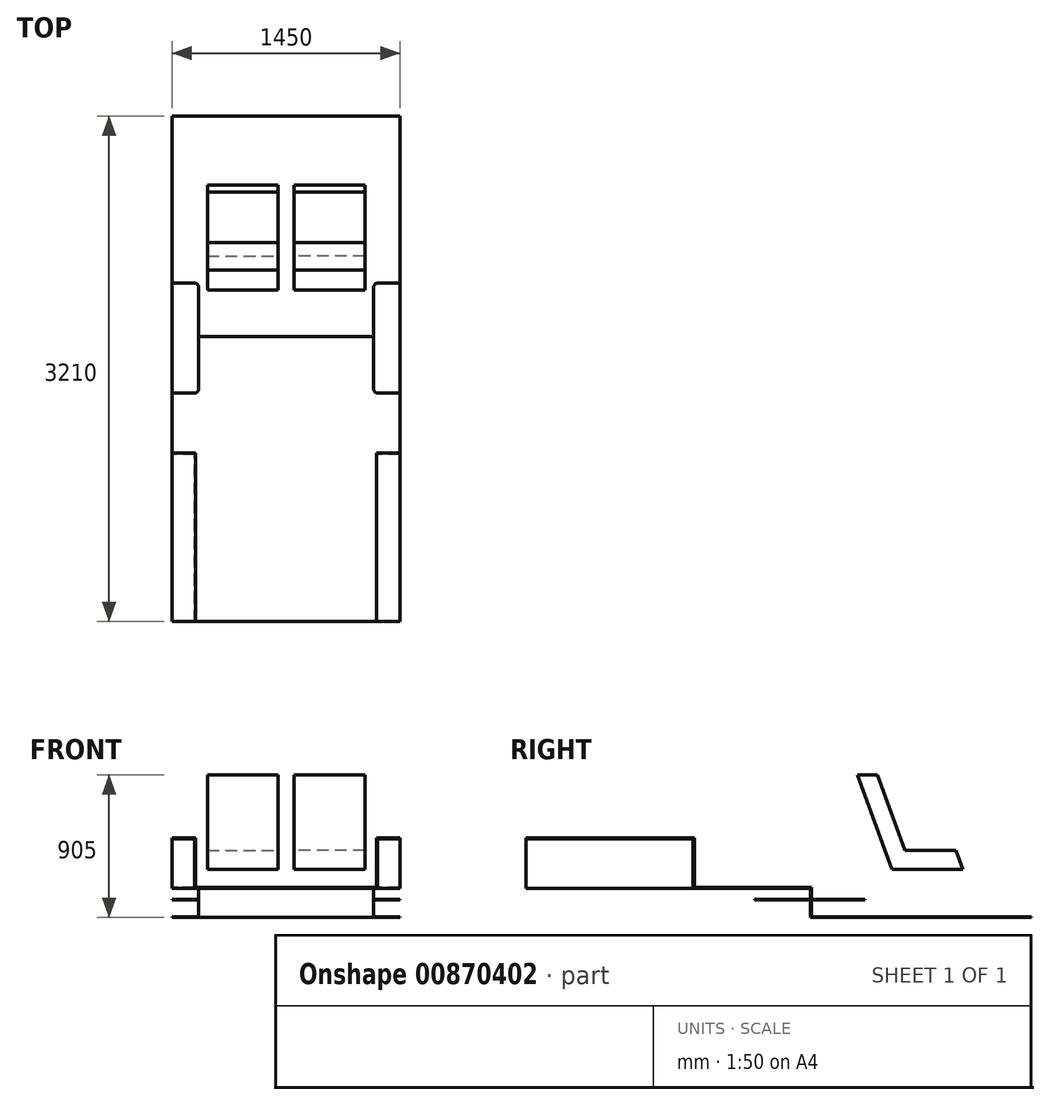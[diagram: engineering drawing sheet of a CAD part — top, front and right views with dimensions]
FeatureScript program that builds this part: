
annotation { "Feature Type Name" : "Feature", "Feature Type Description" : "" }
export const myFeature = defineFeature(function(context is Context, id is Id, definition is map)
    precondition{}
    {
        {
            var Q0;
            Q0=qCreatedBy(makeId("Front.planeOp"),FACE);
            cPlane(context, id + "F0", {"entities" : qUnion([Q0]), "cplaneType" : CPlaneType.OFFSET, "offset" : 750 * mm, "oppositeDirection" : true, "width" : 150 * mm, "height" : 150 * mm});
        }
        {
            var Q0;
            Q0=qCreatedBy(makeId("Front.planeOp"),FACE);
            cPlane(context, id + "F1", {"entities" : qUnion([Q0]), "cplaneType" : CPlaneType.OFFSET, "offset" : 1400 * mm, "width" : 150 * mm, "height" : 150 * mm});
        }
        {
            var Q0;
            Q0=qCreatedBy(makeId("Front.planeOp"),FACE);
            var sketch = newSketch(context, id + "F2", { "sketchPlane" : qUnion([Q0])});
            skLineSegment(sketch, "E0", {"start": v(-725, 0) * mm, "end": v(-575, 0) * mm});
            skLineSegment(sketch, "E1", {"start": v(-575, 0) * mm, "end": v(-575, -315) * mm});
            skLineSegment(sketch, "E2", {"start": v(-575, -315) * mm, "end": v(0, -315) * mm});
            skLineSegment(sketch, "E3", {"start": v(0, 0) * mm, "end": v(0, -315) * mm, "construction": true});
            skLineSegment(sketch, "E4.MirrorCS", {"start": v(575, 0) * mm, "end": v(575, -315) * mm});
            skLineSegment(sketch, "E5.MirrorCS", {"start": v(575, -315) * mm, "end": v(0, -315) * mm});
            skLineSegment(sketch, "E6.MirrorCS", {"start": v(725, 0) * mm, "end": v(575, 0) * mm});
            skLineSegment(sketch, "E7.0", {"start": v(725, -5) * mm, "end": v(580, -5) * mm});
            skLineSegment(sketch, "E7.1", {"start": v(580, -5) * mm, "end": v(580, -320) * mm});
            skLineSegment(sketch, "E7.2", {"start": v(-725, -5) * mm, "end": v(-580, -5) * mm});
            skLineSegment(sketch, "E7.3", {"start": v(-580, -5) * mm, "end": v(-580, -320) * mm});
            skLineSegment(sketch, "E7.4", {"start": v(-580, -320) * mm, "end": v(0, -320) * mm});
            skLineSegment(sketch, "E7.5", {"start": v(580, -320) * mm, "end": v(0, -320) * mm});
            skLineSegment(sketch, "E8", {"start": v(-725, -5) * mm, "end": v(-725, 0) * mm});
            skLineSegment(sketch, "E9", {"start": v(725, -5) * mm, "end": v(725, 0) * mm});
            skSolve(sketch);
        }
        {
            var Q0;
            Q0=makeQuery(id+"F2.imprint","IMPRINT",FACE,{"disambiguationData":[TD([[makeQuery(id+"F2.imprint","IMPRINT",EDGE,{"derivedFrom":sQuery(id+"F2.wireOp",EDGE,"E0")}),-1.0]])]});
            extrude(context, id + "F3", {"entities" : qUnion([Q0]), "depth" : 1060 * mm, "offsetDistance" : 25 * mm});
        }
        {
            var Q0;
            Q0=makeQuery(id+"F3.opExtrude","CAP_FACE",FACE,{"disambiguationData":[OSD([sQuery(id+"F2.wireOp",EDGE,"E0"),sQuery(id+"F2.wireOp",EDGE,"E1"),sQuery(id+"F2.wireOp",EDGE,"E2"),sQuery(id+"F2.wireOp",EDGE,"E4.MirrorCS"),sQuery(id+"F2.wireOp",EDGE,"E5.MirrorCS"),sQuery(id+"F2.wireOp",EDGE,"E6.MirrorCS"),sQuery(id+"F2.wireOp",EDGE,"E7.0"),sQuery(id+"F2.wireOp",EDGE,"E7.1"),sQuery(id+"F2.wireOp",EDGE,"E7.2"),sQuery(id+"F2.wireOp",EDGE,"E7.3"),sQuery(id+"F2.wireOp",EDGE,"E7.4"),sQuery(id+"F2.wireOp",EDGE,"E7.5"),sQuery(id+"F2.wireOp",EDGE,"E8"),sQuery(id+"F2.wireOp",EDGE,"E9")])],"isStart":true});
            var sketch = newSketch(context, id + "F4", { "sketchPlane" : qUnion([Q0])});
            skLineSegment(sketch, "E10", {"start": v(-725, 0) * mm, "end": v(-725, -320) * mm});
            skLineSegment(sketch, "E11", {"start": v(-725, -320) * mm, "end": v(725, -320) * mm});
            skLineSegment(sketch, "E12", {"start": v(725, -320) * mm, "end": v(725, 0) * mm});
            skLineSegment(sketch, "E13", {"start": v(725, 0) * mm, "end": v(575, 0) * mm});
            skLineSegment(sketch, "E14", {"start": v(575, 0) * mm, "end": v(575, -315) * mm});
            skLineSegment(sketch, "E15", {"start": v(575, -315) * mm, "end": v(-575, -315) * mm});
            skLineSegment(sketch, "E16", {"start": v(-575, -315) * mm, "end": v(-575, 0) * mm});
            skLineSegment(sketch, "E17", {"start": v(-575, 0) * mm, "end": v(-725, 0) * mm});
            skSolve(sketch);
        }
        {
            var Q0;
            Q0 = qSketchRegion(id + "F4", true);
            extrude(context, id + "F5", {"entities" : qUnion([Q0]), "operationType" : NewBodyOperationType.ADD, "depth" : 10 * mm, "offsetDistance" : 25 * mm});
        }
        {
            var Q0;
            Q0=makeQuery(id+"F5.opExtrude","CAP_FACE",FACE,{"disambiguationData":[OSD([sQuery(id+"F4.wireOp",EDGE,"E10"),sQuery(id+"F4.wireOp",EDGE,"E11"),sQuery(id+"F4.wireOp",EDGE,"E12"),sQuery(id+"F4.wireOp",EDGE,"E13"),sQuery(id+"F4.wireOp",EDGE,"E14"),sQuery(id+"F4.wireOp",EDGE,"E15"),sQuery(id+"F4.wireOp",EDGE,"E16"),sQuery(id+"F4.wireOp",EDGE,"E17")])],"isStart":false});
            var sketch = newSketch(context, id + "F6", { "sketchPlane" : qUnion([Q0])});
            skLineSegment(sketch, "E18.bottom", {"start": v(-725, -320) * mm, "end": v(725, -320) * mm});
            skLineSegment(sketch, "E18.top", {"start": v(-725, -315) * mm, "end": v(725, -315) * mm});
            skLineSegment(sketch, "E18.left", {"start": v(-725, -320) * mm, "end": v(-725, -315) * mm});
            skLineSegment(sketch, "E18.right", {"start": v(725, -320) * mm, "end": v(725, -315) * mm});
            skSolve(sketch);
        }
        {
            var Q0;
            Q0 = qSketchRegion(id + "F6", true);
            var Q1;
            Q1=qCreatedBy(id+"F0.planeOp",FACE);
            extrude(context, id + "F7", {"entities" : qUnion([Q0]), "operationType" : NewBodyOperationType.ADD, "endBound" : BoundingType.UP_TO_SURFACE, "depth" : 25 * mm, "endBoundEntityFace" : qUnion([Q1]), "offsetDistance" : 25 * mm});
        }
        {
            var Q0;
            Q0=qCreatedBy(makeId("Top.planeOp"),FACE);
            cPlane(context, id + "F8", {"entities" : qUnion([Q0]), "cplaneType" : CPlaneType.OFFSET, "offset" : 500 * mm, "oppositeDirection" : true, "width" : 150 * mm, "height" : 150 * mm});
        }
        {
            var Q0;
            Q0=qCreatedBy(makeId("Top.planeOp"),FACE);
            cPlane(context, id + "F9", {"entities" : qUnion([Q0]), "cplaneType" : CPlaneType.OFFSET, "offset" : 300 * mm, "oppositeDirection" : true, "width" : 150 * mm, "height" : 150 * mm});
        }
        {
            var Q0;
            Q0=qCreatedBy(makeId("Right.planeOp"),FACE);
            var sketch = newSketch(context, id + "F10", { "sketchPlane" : qUnion([Q0])});
            skLineSegment(sketch, "E19", {"start": v(750, -315) * mm, "end": v(750, -500) * mm});
            skLineSegment(sketch, "E20", {"start": v(750, -500) * mm, "end": v(2150, -500) * mm});
            skLineSegment(sketch, "E21", {"start": v(750, -315) * mm, "end": v(745, -315) * mm});
            skLineSegment(sketch, "E22", {"start": v(745, -315) * mm, "end": v(745, -505) * mm});
            skLineSegment(sketch, "E23", {"start": v(745, -505) * mm, "end": v(2150, -505) * mm});
            skLineSegment(sketch, "E24", {"start": v(2150, -505) * mm, "end": v(2150, -500) * mm});
            skSolve(sketch);
        }
        {
            var Q0;
            Q0=qCreatedBy(makeId("Right.planeOp"),FACE);
            var sketch = newSketch(context, id + "F11", { "sketchPlane" : qUnion([Q0])});
            skLineSegment(sketch, "E25", {"start": v(3466, -500) * mm, "end": v(3466, 197.75) * mm});
            skLineSegment(sketch, "E26", {"start": v(3466, 197.75) * mm, "end": v(2488, 459.8) * mm});
            skLineSegment(sketch, "E27", {"start": v(2488, 459.8) * mm, "end": v(1490, 1036) * mm});
            skLineSegment(sketch, "E28", {"start": v(1490, 1036) * mm, "end": v(-1262.6, 1036) * mm});
            skLineSegment(sketch, "E29", {"start": v(-1262.6, 1036) * mm, "end": v(-1410, 200) * mm});
            skLineSegment(sketch, "E30", {"start": v(-1410, 200) * mm, "end": v(-1410, -500) * mm});
            skLineSegment(sketch, "E31", {"start": v(-1410, -500) * mm, "end": v(3466, -500) * mm});
            skCircle(sketch, "E32", {"center": v(2588, -450) * mm, "radius": 350 * mm});
            skCircle(sketch, "E33", {"center": v(-418, -450) * mm, "radius": 350 * mm});
            skLineSegment(sketch, "E34", {"start": v(-1160, 200) * mm, "end": v(-1160, -500) * mm});
            skLineSegment(sketch, "E35.bottom", {"start": v(390, -500) * mm, "end": v(1090, -500) * mm});
            skLineSegment(sketch, "E35.top", {"start": v(390, 800) * mm, "end": v(1090, 800) * mm});
            skLineSegment(sketch, "E35.left", {"start": v(390, -500) * mm, "end": v(390, 800) * mm});
            skLineSegment(sketch, "E35.right", {"start": v(1090, -500) * mm, "end": v(1090, 800) * mm});
            skLineSegment(sketch, "E36", {"start": v(-1098.9, 915) * mm, "end": v(116.64, 915) * mm});
            skSolve(sketch);
        }
        {
            var Q0;
            Q0=makeQuery(id+"F10.imprint","IMPRINT",FACE,{"disambiguationData":[TD([[makeQuery(id+"F10.imprint","IMPRINT",EDGE,{"derivedFrom":sQuery(id+"F10.wireOp",EDGE,"E19")}),-1.0]])]});
            var Q1;
            Q1=makeQuery(id+"F7.boolean.opBoolean","MERGE",FACE,{"derivedFrom":[makeQuery(id+"F5.boolean.opBoolean","MERGE",FACE,{"derivedFrom":[makeQuery(id+"F3.opExtrude","SWEPT_FACE",FACE,{"disambiguationData":[OSD([sQuery(id+"F2.wireOp",EDGE,"E9")])]}),makeQuery(id+"F5.opExtrude","SWEPT_FACE",FACE,{"disambiguationData":[OSD([sQuery(id+"F4.wireOp",EDGE,"E10")])]})]}),makeQuery(id+"F7.opExtrude","SWEPT_FACE",FACE,{"disambiguationData":[OSD([sQuery(id+"F6.wireOp",EDGE,"E18.left")])]})]});
            var Q2;
            Q2=makeQuery(id+"F7.boolean.opBoolean","MERGE",FACE,{"derivedFrom":[makeQuery(id+"F5.boolean.opBoolean","MERGE",FACE,{"derivedFrom":[makeQuery(id+"F3.opExtrude","SWEPT_FACE",FACE,{"disambiguationData":[OSD([sQuery(id+"F2.wireOp",EDGE,"E8")])]}),makeQuery(id+"F5.opExtrude","SWEPT_FACE",FACE,{"disambiguationData":[OSD([sQuery(id+"F4.wireOp",EDGE,"E12")])]})]}),makeQuery(id+"F7.opExtrude","SWEPT_FACE",FACE,{"disambiguationData":[OSD([sQuery(id+"F6.wireOp",EDGE,"E18.right")])]})]});
            extrude(context, id + "F12", {"entities" : qUnion([Q0]), "operationType" : NewBodyOperationType.ADD, "endBound" : BoundingType.UP_TO_SURFACE, "depth" : 25 * mm, "endBoundEntityFace" : qUnion([Q1]), "offsetDistance" : 25 * mm, "hasSecondDirection" : true, "secondDirectionBound" : SecondDirectionBoundingType.UP_TO_SURFACE, "secondDirectionOppositeDirection" : true, "secondDirectionDepth" : 25 * mm, "secondDirectionBoundEntityFace" : qUnion([Q2])});
        }
        {
            var Q0;
            Q0=qCreatedBy(id+"F9.planeOp",FACE);
            var sketch = newSketch(context, id + "F13", { "sketchPlane" : qUnion([Q0])});
            skLineSegment(sketch, "E37.bottom", {"start": v(725, 390) * mm, "end": v(585, 390) * mm});
            skLineSegment(sketch, "E37.top", {"start": v(725, 1090) * mm, "end": v(585, 1090) * mm});
            skLineSegment(sketch, "E37.left", {"start": v(725, 390) * mm, "end": v(725, 1090) * mm});
            skLineSegment(sketch, "E37.right", {"start": v(555, 420) * mm, "end": v(555, 1060) * mm});
            skPoint(sketch, "E38.visualSharp", {"position": v(555, 390) * mm});
            skArc(sketch, "E38.filletArc", {"start": v(555, 420) * mm, "mid": v(563.79, 398.79) * mm, "end": v(585, 390) * mm});
            skPoint(sketch, "E39.visualSharp", {"position": v(555, 1090) * mm});
            skArc(sketch, "E39.filletArc", {"start": v(585, 1090) * mm, "mid": v(563.79, 1081.21) * mm, "end": v(555, 1060) * mm});
            skArc(sketch, "E40.MirrorCS", {"start": v(-585, 1090) * mm, "mid": v(-563.79, 1081.21) * mm, "end": v(-555, 1060) * mm});
            skArc(sketch, "E41.MirrorCS", {"start": v(-555, 420) * mm, "mid": v(-563.79, 398.79) * mm, "end": v(-585, 390) * mm});
            skPoint(sketch, "E42.MirrorP", {"position": v(-555, 1090) * mm});
            skLineSegment(sketch, "E43.MirrorCS", {"start": v(-555, 420) * mm, "end": v(-555, 1060) * mm});
            skLineSegment(sketch, "E44.MirrorCS", {"start": v(-725, 390) * mm, "end": v(-585, 390) * mm});
            skLineSegment(sketch, "E45.MirrorCS", {"start": v(-725, 390) * mm, "end": v(-725, 1090) * mm});
            skLineSegment(sketch, "E46.MirrorCS", {"start": v(-725, 1090) * mm, "end": v(-585, 1090) * mm});
            skPoint(sketch, "E47.MirrorP", {"position": v(-555, 390) * mm});
            skSolve(sketch);
        }
        {
            var Q0;
            Q0 = qSketchRegion(id + "F13", true);
            var Q1;
            Q1=makeQuery(id+"F12.opExtrude","SWEPT_FACE",FACE,{"disambiguationData":[OSD([sQuery(id+"F10.wireOp",EDGE,"E23")])]});
            extrude(context, id + "F14", {"entities" : qUnion([Q0]), "operationType" : NewBodyOperationType.REMOVE, "endBound" : BoundingType.UP_TO_SURFACE, "oppositeDirection" : true, "depth" : 25 * mm, "endBoundEntityFace" : qUnion([Q1]), "offsetDistance" : 25 * mm});
        }
        {
            var Q0;
            Q0 = qSketchRegion(id + "F13", true);
            var Q1;
            Q1=makeQuery(id+"F7.boolean.opBoolean","MERGE",FACE,{"derivedFrom":[makeQuery(id+"F5.boolean.opBoolean","MERGE",FACE,{"derivedFrom":[makeQuery(id+"F3.opExtrude","SWEPT_FACE",FACE,{"disambiguationData":[OSD([sQuery(id+"F2.wireOp",EDGE,"E2"),sQuery(id+"F2.wireOp",EDGE,"E5.MirrorCS")])]}),makeQuery(id+"F5.opExtrude","SWEPT_FACE",FACE,{"disambiguationData":[OSD([sQuery(id+"F4.wireOp",EDGE,"E15")])]})]}),makeQuery(id+"F7.opExtrude","SWEPT_FACE",FACE,{"disambiguationData":[OSD([sQuery(id+"F6.wireOp",EDGE,"E18.top")])]})]});
            var Q2;
            Q2=makeQuery(id+"F7.boolean.opBoolean","MERGE",FACE,{"derivedFrom":[makeQuery(id+"F5.boolean.opBoolean","MERGE",FACE,{"derivedFrom":[makeQuery(id+"F3.opExtrude","SWEPT_FACE",FACE,{"disambiguationData":[OSD([sQuery(id+"F2.wireOp",EDGE,"E2"),sQuery(id+"F2.wireOp",EDGE,"E5.MirrorCS")])]}),makeQuery(id+"F5.opExtrude","SWEPT_FACE",FACE,{"disambiguationData":[OSD([sQuery(id+"F4.wireOp",EDGE,"E15")])]})]}),makeQuery(id+"F7.opExtrude","SWEPT_FACE",FACE,{"disambiguationData":[OSD([sQuery(id+"F6.wireOp",EDGE,"E18.top")])]})]});
            extrude(context, id + "F15", {"entities" : qUnion([Q0]), "operationType" : NewBodyOperationType.ADD, "endBound" : BoundingType.UP_TO_SURFACE, "oppositeDirection" : true, "depth" : 5 * mm, "endBoundEntityFace" : qUnion([Q1]), "hasOffset" : true, "offsetDistance" : 80 * mm, "offsetOppositeDirection" : true, "hasSecondDirection" : true, "secondDirectionBound" : SecondDirectionBoundingType.UP_TO_SURFACE, "secondDirectionOppositeDirection" : true, "secondDirectionDepth" : 25 * mm, "secondDirectionBoundEntityFace" : qUnion([Q2]), "hasSecondDirectionOffset" : true, "secondDirectionOffsetDistance" : 75 * mm, "secondDirectionOffsetOppositeDirection" : true});
        }
        {
            var Q0;
            Q0=qCreatedBy(makeId("Right.planeOp"),FACE);
            var sketch = newSketch(context, id + "F16", { "sketchPlane" : qUnion([Q0])});
            skLineSegment(sketch, "E48", {"start": v(1043.81, 400) * mm, "end": v(1262.2, -200) * mm});
            skLineSegment(sketch, "E49", {"start": v(1262.2, -200) * mm, "end": v(1712.2, -200) * mm});
            skLineSegment(sketch, "E50", {"start": v(1712.2, -200) * mm, "end": v(1668.52, -80) * mm});
            skLineSegment(sketch, "E51", {"start": v(1668.52, -80) * mm, "end": v(1346.22, -80) * mm});
            skLineSegment(sketch, "E52", {"start": v(1346.22, -80) * mm, "end": v(1171.51, 400) * mm});
            skLineSegment(sketch, "E53", {"start": v(1171.51, 400) * mm, "end": v(1043.81, 400) * mm});
            skSolve(sketch);
        }
        {
            var Q0;
            Q0=makeQuery(id+"F16.imprint","IMPRINT",FACE,{"disambiguationData":[TD([[makeQuery(id+"F16.imprint","IMPRINT",EDGE,{"derivedFrom":sQuery(id+"F16.wireOp",EDGE,"E48")}),1.0]])]});
            var Q1;
            Q1=qCreatedBy(makeId("Right.planeOp"),FACE);
            extrude(context, id + "F17", {"entities" : qUnion([Q0]), "endBound" : BoundingType.UP_TO_SURFACE, "depth" : 25 * mm, "endBoundEntityFace" : qUnion([Q1]), "hasOffset" : true, "offsetDistance" : 500 * mm, "offsetOppositeDirection" : true, "hasSecondDirection" : true, "secondDirectionOppositeDirection" : false, "secondDirectionDepth" : 50 * mm});
        }
        {
            var Q0;
            Q0=makeQuery(id+"F17.opExtrude","SWEPT_BODY",BODY,{"disambiguationData":[OSD([sQuery(id+"F16.wireOp",EDGE,"E48"),sQuery(id+"F16.wireOp",EDGE,"E49"),sQuery(id+"F16.wireOp",EDGE,"E50"),sQuery(id+"F16.wireOp",EDGE,"E51"),sQuery(id+"F16.wireOp",EDGE,"E52"),sQuery(id+"F16.wireOp",EDGE,"E53")])]});
            var Q1;
            Q1=qCreatedBy(makeId("Right.planeOp"),FACE);
            mirror(context, id + "F18", {"entities" : qUnion([Q0]), "mirrorPlane" : qUnion([Q1])});
        }
    });
